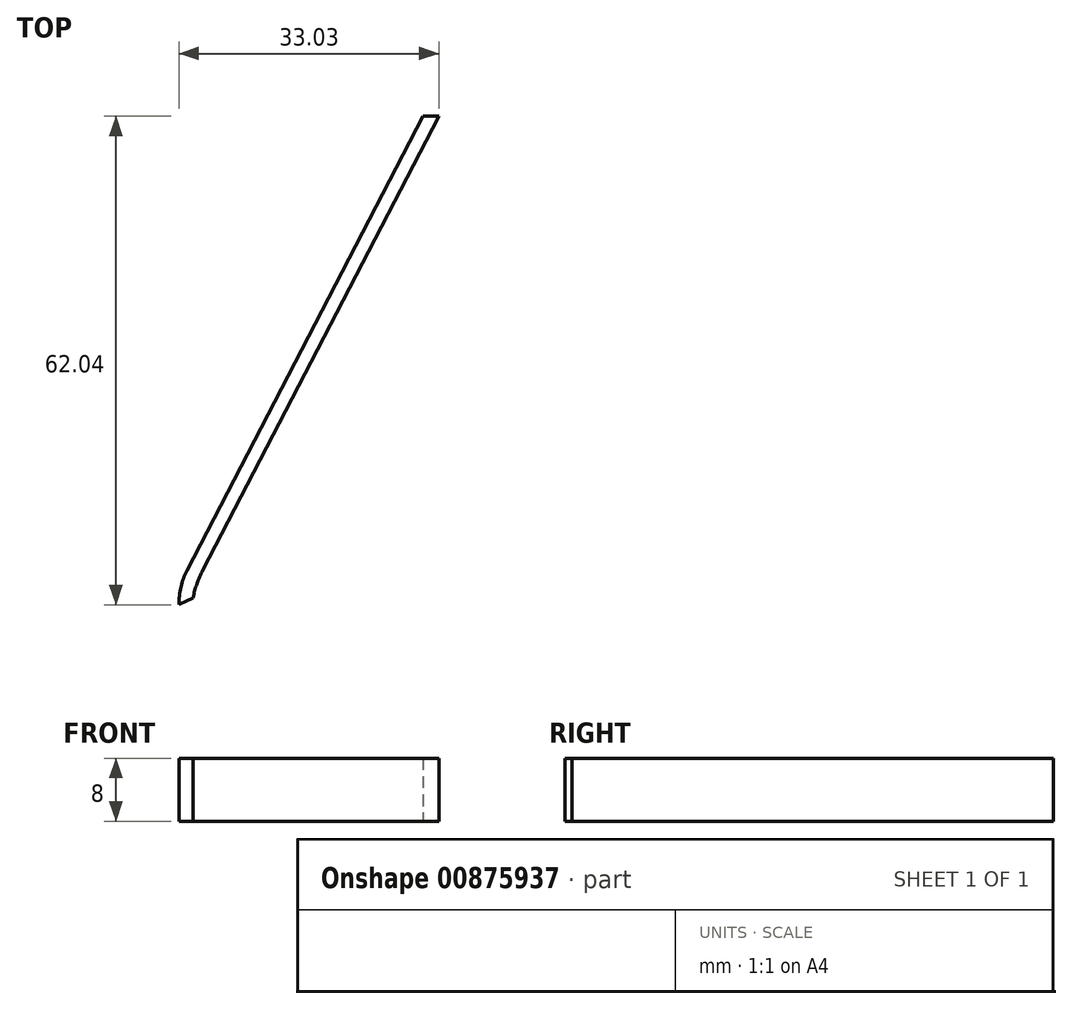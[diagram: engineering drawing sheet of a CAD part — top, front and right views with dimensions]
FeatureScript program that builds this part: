
annotation { "Feature Type Name" : "Feature", "Feature Type Description" : "" }
export const myFeature = defineFeature(function(context is Context, id is Id, definition is map)
    precondition{}
    {
        {
            var Q0;
            Q0=qCreatedBy(makeId("Top.planeOp"),FACE);
            var sketch = newSketch(context, id + "F0", { "sketchPlane" : qUnion([Q0])});
            skLineSegment(sketch, "E0", {"start": v(1.23, 17.05) * mm, "end": v(3.23, 17.05) * mm});
            skLineSegment(sketch, "E1", {"start": v(3.23, 17.05) * mm, "end": v(33.23, 74.71) * mm});
            skLineSegment(sketch, "E2", {"start": v(1.23, 17.05) * mm, "end": v(31.23, 74.71) * mm});
            skLineSegment(sketch, "E3", {"start": v(31.23, 74.71) * mm, "end": v(33.23, 74.71) * mm});
            skArc(sketch, "E4", {"start": v(3.23, 17.05) * mm, "mid": v(2.5, 15.34) * mm, "end": v(2, 13.55) * mm});
            skLineSegment(sketch, "E5", {"start": v(2, 13.55) * mm, "end": v(0.2, 12.67) * mm});
            skArc(sketch, "E6", {"start": v(1.23, 17.05) * mm, "mid": v(0.45, 14.92) * mm, "end": v(0.2, 12.67) * mm});
            skSolve(sketch);
        }
        {
            var Q0;
            Q0=makeQuery(id+"F0.imprint","IMPRINT",FACE,{"disambiguationData":[TD([[makeQuery(id+"F0.imprint","IMPRINT",EDGE,{"derivedFrom":sQuery(id+"F0.wireOp",EDGE,"E0")}),1.0]])]});
            var Q1;
            Q1=makeQuery(id+"F0.imprint","IMPRINT",FACE,{"disambiguationData":[TD([[makeQuery(id+"F0.imprint","IMPRINT",EDGE,{"derivedFrom":sQuery(id+"F0.wireOp",EDGE,"E0")}),-1.0]])]});
            extrude(context, id + "F1", {"entities" : qUnion([Q0, Q1]), "depth" : 6 * mm, "offsetDistance" : 25 * mm});
        }
        {
            var Q0;
            Q0=makeQuery(id+"F0.imprint","IMPRINT",FACE,{"disambiguationData":[TD([[makeQuery(id+"F0.imprint","IMPRINT",EDGE,{"derivedFrom":sQuery(id+"F0.wireOp",EDGE,"E0")}),1.0]])]});
            var Q1;
            Q1=makeQuery(id+"F0.imprint","IMPRINT",FACE,{"disambiguationData":[TD([[makeQuery(id+"F0.imprint","IMPRINT",EDGE,{"derivedFrom":sQuery(id+"F0.wireOp",EDGE,"E0")}),-1.0]])]});
            extrude(context, id + "F2", {"entities" : qUnion([Q0, Q1]), "operationType" : NewBodyOperationType.ADD, "depth" : 8 * mm, "offsetDistance" : 25 * mm});
        }
    });
